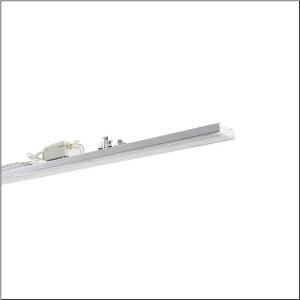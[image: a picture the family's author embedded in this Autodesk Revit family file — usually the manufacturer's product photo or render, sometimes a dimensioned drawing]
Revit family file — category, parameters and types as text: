
# Revit family: licross_21_recessed_mo_52te14cn485g
name_source: partatom
category: Lighting Fixtures
units: mm (PartAtom-declared; Revit-internal decimal feet)

## family parameters
Cut with Voids When Loaded = No
Host = Face
Light Source = No
Part Type = Normal
Room Calculation Point = No
Round Connector Dimension = Use Diameter
Shared = No

## types (1)
- --- (1 x LED, 8530 lm, 49.9 W, 4000K)
    Apparent Load = 50 VA
    CIE Flux Codes = 56 84 97 100 100
    Color Rendering = 80
    Color Temperature = 4000K
    Default Elevation = 1800 mm
    Description = Licross 21 Recessed MO, luminaire insert, of sheet steel, galvanised, coil coated, white, length: 1.500mm, width: 66mm, height: 67mm, LED rated luminous flux: 8.530lm, light colour: 840, SDCM (Standard Deviation of Colour Matching)MacAdam ≤ 3 SDCM (initial), control gear: ON/OFF Multilumen, CLOi, with plug, 5-pole, with phase selection, mains connection: 220..240V, AC, 50/60Hz, start of lifetime: 50W, end of service life: 61W, internal wiring halogen-free, primary light control with lens, of plastic, primary optical cover: cover, of PMMA, light emission: direct distribution, primary light characteristic: asymmetric, protection rating (complete): IP54, insulation class (complete): insulation class I (protective earthing), certification: CE, ENEC, VDE, UKCA, protection symbol: D if used in an environment with non-conductive dust loads with corresponding accessories, impact resistance: IK06, permissible ambient temperature for indoor applications: -35..+40°C, corresponds to IFS (International Featured Standards) requirements for safety and quality in the food industry, reducing of maximum allowable ambient temperature of 5°C with ceiling mounting, LABS conformity tested according to VDMA 24364:2018-05, The light source and the operating device comply with the requirements of the Ecodesign Regulation (EU) 2019/2020 and are replaceable in accordance with this regulation, packaging unit: 1 piece
    Height = 58 mm
    Lamp = 1 x LED
    Lamp Light Flux = 8530 lm
    Lamp Power = 49.9 W
    Lamp count = 1
    Length = 1500 mm
    Luminous efficacy = 171 lm/W
    Manufacturer = Siteco
    ModVariant = No
    Model = 52TE14CN485G
    Mounting Place = Ceiling
    Mounting Type = Pendant
    Number of Poles = 1
    OnlyDefault = Yes
    Power Factor = 1
    Product Name = Licross 21 Recessed MO
    Product group = luminaire insert | ceiling pendant
    ProductGroupID = 901
    Protection Class = Protection class I
    Protection Degree = IP 54
    RLX_Detail_Level = 1
    RLX_Emergency_Light_Flux = 0 lm
    RLX_Emergency_Type = 0
    RLX_Emergency_Type_DB = No
    RlxData = <blob elided: 23045 chars, md5=072639ab>
    Socket = socket
    Standby Power = 0 W
    System Light Flux = 8530 lm
    System Power = 50 W
    Type Comments = factory setting: luminous flux: 100 % | (A | C | E) | 116 mA
    Type Image = l_1296930.jpg
    URL = http://relux.com
    VarID = @adj_112269
    Voltage = 0 V
    Weight = 0.00 kg
    Width = 66 mm

## geometry (parser evidence)
native form markers: Blend x4, Sweep x11
no freeform markers — native parametric forms only
